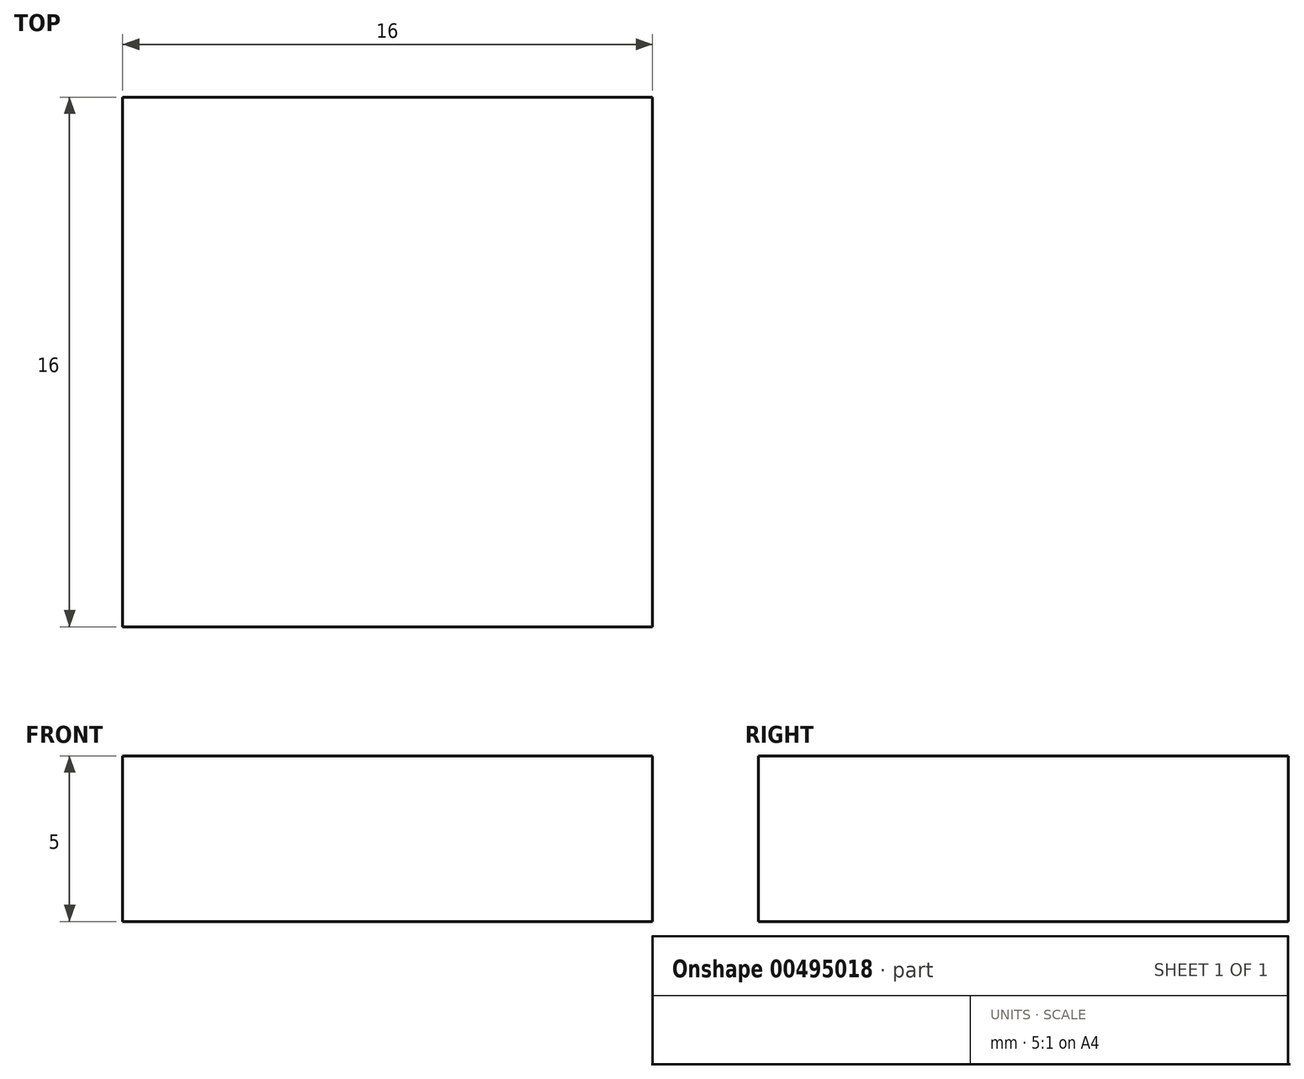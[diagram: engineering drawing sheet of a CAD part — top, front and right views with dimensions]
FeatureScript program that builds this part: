
annotation { "Feature Type Name" : "Feature", "Feature Type Description" : "" }
export const myFeature = defineFeature(function(context is Context, id is Id, definition is map)
    precondition{}
    {
        {
            var Q0;
            Q0=qCreatedBy(makeId("Top.planeOp"),FACE);
            var sketch = newSketch(context, id + "F0", { "sketchPlane" : qUnion([Q0])});
            skLineSegment(sketch, "E0.bottom", {"start": v(8, 8) * mm, "end": v(-8, 8) * mm});
            skLineSegment(sketch, "E0.top", {"start": v(8, -8) * mm, "end": v(-8, -8) * mm});
            skLineSegment(sketch, "E0.left", {"start": v(8, 8) * mm, "end": v(8, -8) * mm});
            skLineSegment(sketch, "E0.right", {"start": v(-8, 8) * mm, "end": v(-8, -8) * mm});
            skPoint(sketch, "E0.middle", {"position": v(0, 0) * mm});
            skSolve(sketch);
        }
        {
            var Q0;
            Q0=makeQuery(id+"F0.imprint","IMPRINT",FACE,{"disambiguationData":[TD([[makeQuery(id+"F0.imprint","IMPRINT",EDGE,{"derivedFrom":sQuery(id+"F0.wireOp",EDGE,"E0.bottom")}),1.0]])]});
            extrude(context, id + "F1", {"entities" : qUnion([Q0]), "depth" : 5 * mm, "offsetDistance" : 25.4 * mm});
        }
    });
